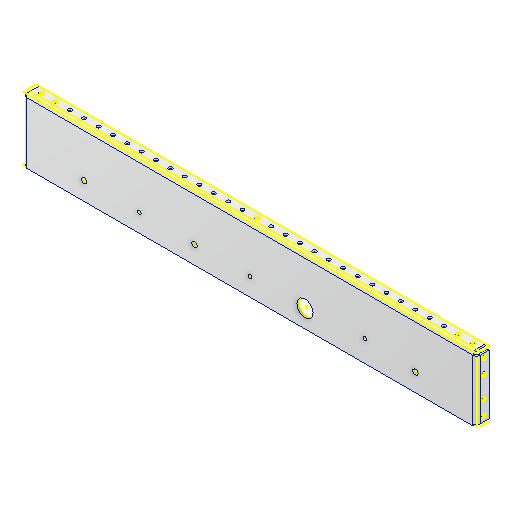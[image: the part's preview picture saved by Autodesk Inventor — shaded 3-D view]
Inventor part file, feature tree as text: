
AUTODESK INVENTOR PART (.ipt)
format: ipt  version: 2022 (Build 260153000, 153)  size: 309,760 bytes
history: native  units: in
note: dims shown in document units (in); Inventor stores cm internally (conversion verified against a paired STEP export)
features: sketch x10, other x4
ambient origin geometry x8: Origin, YZ Plane, XZ Plane, XY Plane, X Axis, Y Axis, Z Axis, Center Point
bodies: Solid1 (feature_tree)
feature tree (14):
  other  "side pannel 1 00001"
  other  "Solid1::side pannel 1 00001"
  other  "TaggingFeature1"
  sketch  "Sketch2"  dims[d0=0.3937in]
  sketch  "Sketch3"  dims[d1=0.125in]
  sketch  "Sketch6"
  sketch  "Sketch9"
  sketch  "Sketch10"
  sketch  "Sketch11"
  sketch  "Sketch12"
  sketch  "Sketch13"
  sketch  "Sketch14"
  sketch  "Sketch15"
  other  "Definition1"
